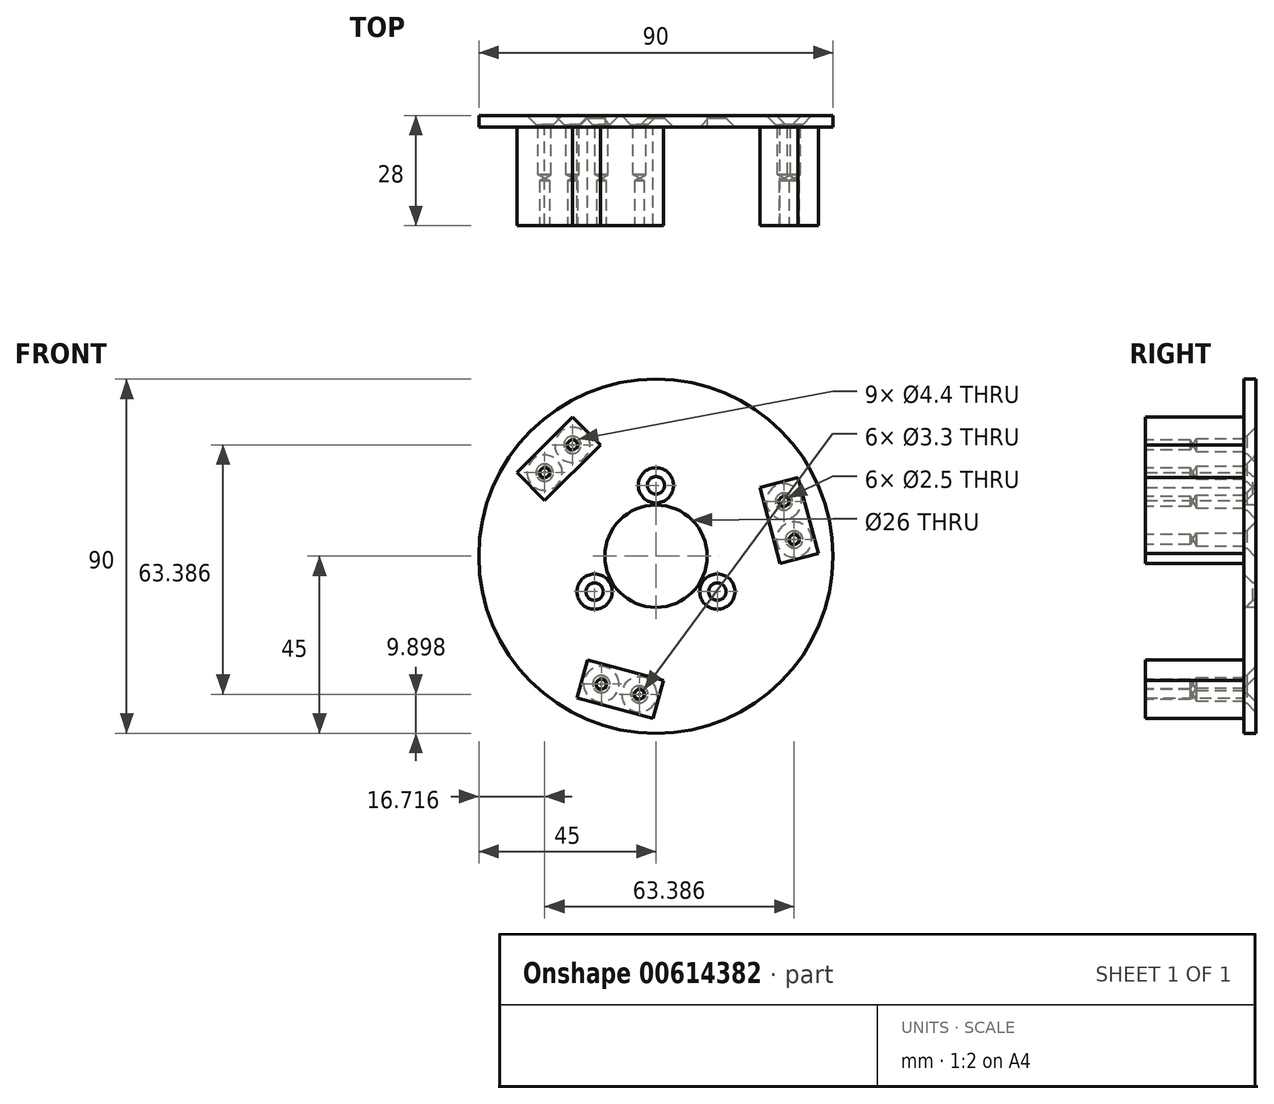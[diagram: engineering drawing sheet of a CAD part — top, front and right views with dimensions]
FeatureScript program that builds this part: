
annotation { "Feature Type Name" : "Feature", "Feature Type Description" : "" }
export const myFeature = defineFeature(function(context is Context, id is Id, definition is map)
    precondition{}
    {
        {
            var Q0;
            Q0=qCreatedBy(makeId("Front.planeOp"),FACE);
            var sketch = newSketch(context, id + "F0", { "sketchPlane" : qUnion([Q0])});
            skCircle(sketch, "E0", {"center": v(0, 0) * mm, "radius": 13 * mm});
            skCircle(sketch, "E1", {"center": v(0, 0) * mm, "radius": 45 * mm});
            skCircle(sketch, "E2", {"center": v(0, 0) * mm, "radius": 23 * mm, "construction": true});
            skLineSegment(sketch, "E3", {"start": v(0, 23) * mm, "end": v(0, 13) * mm, "construction": true});
            skPoint(sketch, "E4", {"position": v(0, 18) * mm});
            skPoint(sketch, "E5.1.0", {"position": v(-15.59, -9) * mm});
            skPoint(sketch, "E5.2.0", {"position": v(15.59, -9) * mm});
            skLineSegment(sketch, "E6", {"start": v(0, 0) * mm, "end": v(-31.82, 31.82) * mm, "construction": true});
            skCircle(sketch, "E7", {"center": v(0, 0) * mm, "radius": 25 * mm, "construction": true});
            skCircle(sketch, "E8", {"center": v(0, 0) * mm, "radius": 18.5 * mm, "construction": true});
            skPoint(sketch, "E9", {"position": v(-21.21, 28.28) * mm});
            skPoint(sketch, "E10.MirrorP", {"position": v(-28.28, 21.21) * mm});
            skLineSegment(sketch, "E11", {"start": v(-28.28, 21.21) * mm, "end": v(-21.21, 28.28) * mm});
            skPoint(sketch, "E12", {"position": v(-24.75, 24.75) * mm});
            skPoint(sketch, "E13.1.0", {"position": v(-9.06, -33.8) * mm});
            skPoint(sketch, "E13.1.1", {"position": v(-13.89, -32.51) * mm});
            skPoint(sketch, "E13.1.2", {"position": v(-4.23, -35.1) * mm});
            skPoint(sketch, "E13.2.0", {"position": v(33.8, 9.06) * mm});
            skPoint(sketch, "E13.2.1", {"position": v(35.1, 4.23) * mm});
            skPoint(sketch, "E13.2.2", {"position": v(32.51, 13.89) * mm});
            skSolve(sketch);
        }
        {
            var Q0;
            Q0=makeQuery(id+"F0.imprint","IMPRINT",FACE,{"disambiguationData":[TD([[makeQuery(id+"F0.imprint","IMPRINT",EDGE,{"derivedFrom":sQuery(id+"F0.wireOp",EDGE,"E0")}),-1.0]])]});
            extrude(context, id + "F1", {"entities" : qUnion([Q0]), "oppositeDirection" : true, "depth" : 3 * mm, "offsetDistance" : 25 * mm});
        }
        {
            var Q0;
            Q0=sQuery(id+"F0.wireOp",VERTEX,"E4");
            var Q1;
            Q1=sQuery(id+"F0.wireOp",VERTEX,"E5.1.0");
            var Q2;
            Q2=sQuery(id+"F0.wireOp",VERTEX,"E5.2.0");
            var Q3;
            Q3=makeQuery(id+"F1.opExtrude","SWEPT_BODY",BODY,{"disambiguationData":[OSD([sQuery(id+"F0.wireOp",EDGE,"E0"),sQuery(id+"F0.wireOp",EDGE,"E1")])]});
            hole(context, id + "F2", {"style" : HoleStyle.C_SINK, "endStyle" : HoleEndStyle.THROUGH, "standardTappedOrClearance" : lookupTablePath({ "standard" : "ISO", "fit" : "Normal", "size" : "M4", "type" : "Clearance" }), "standardBlindInLast" : lookupTablePath({ "fit" : "Standard", "standard" : "ISO", "size" : "M4", "type" : "Clearance" }), "holeDiameter" : 4.4 * mm, "cSinkDiameter" : 8.96 * mm, "cSinkAngle" : 90 * degree, "majorDiameter" : 5 * mm, "isTappedThrough" : true, "tappedDepth" : 12 * mm, "tapClearance" : 3, "locations" : qUnion([Q0, Q1, Q2]), "scope" : qUnion([Q3])});
        }
        {
            var Q0;
            Q0=makeQuery(id+"F1.opExtrude","CAP_FACE",FACE,{"disambiguationData":[OSD([sQuery(id+"F0.wireOp",EDGE,"E0"),sQuery(id+"F0.wireOp",EDGE,"E1")])],"isStart":false});
            var sketch = newSketch(context, id + "F3", { "sketchPlane" : qUnion([Q0])});
            skPoint(sketch, "E14.0", {"position": v(21.21, 28.28) * mm});
            skPoint(sketch, "E15.0", {"position": v(28.28, 21.21) * mm});
            skPoint(sketch, "E16.0", {"position": v(13.89, -32.51) * mm});
            skPoint(sketch, "E17.0", {"position": v(4.23, -35.1) * mm});
            skPoint(sketch, "E18.0", {"position": v(-35.1, 4.23) * mm});
            skPoint(sketch, "E19.0", {"position": v(-32.51, 13.89) * mm});
            skSolve(sketch);
        }
        {
            var Q0;
            Q0=sQuery(id+"F3.wireOp",VERTEX,"E19.0");
            var Q1;
            Q1=sQuery(id+"F3.wireOp",VERTEX,"E18.0");
            var Q2;
            Q2=sQuery(id+"F3.wireOp",VERTEX,"E14.0");
            var Q3;
            Q3=sQuery(id+"F3.wireOp",VERTEX,"E15.0");
            var Q4;
            Q4=sQuery(id+"F3.wireOp",VERTEX,"E16.0");
            var Q5;
            Q5=sQuery(id+"F3.wireOp",VERTEX,"E17.0");
            var Q6;
            Q6=makeQuery(id+"F1.opExtrude","SWEPT_BODY",BODY,{"disambiguationData":[OSD([sQuery(id+"F0.wireOp",EDGE,"E0"),sQuery(id+"F0.wireOp",EDGE,"E1")])]});
            hole(context, id + "F4", {"style" : HoleStyle.C_SINK, "endStyle" : HoleEndStyle.THROUGH, "standardTappedOrClearance" : lookupTablePath({ "standard" : "ISO", "fit" : "Normal", "size" : "M4", "type" : "Clearance" }), "standardBlindInLast" : lookupTablePath({ "fit" : "Standard", "standard" : "ISO", "size" : "M4", "type" : "Clearance" }), "holeDiameter" : 4.4 * mm, "cSinkDiameter" : 8.96 * mm, "cSinkAngle" : 90 * degree, "majorDiameter" : 5 * mm, "isTappedThrough" : true, "tappedDepth" : 12 * mm, "tapClearance" : 3, "locations" : qUnion([Q0, Q1, Q2, Q3, Q4, Q5]), "scope" : qUnion([Q6])});
        }
        {
            var Q0;
            Q0=makeQuery(id+"F0.imprint","IMPRINT",FACE,{"disambiguationData":[TD([[makeQuery(id+"F0.imprint","IMPRINT",EDGE,{"derivedFrom":sQuery(id+"F0.wireOp",EDGE,"E0")}),-1.0]])]});
            var sketch = newSketch(context, id + "F5", { "sketchPlane" : qUnion([Q0])});
            skLineSegment(sketch, "E20", {"start": v(-21.21, 35.36) * mm, "end": v(-35.36, 21.21) * mm});
            skLineSegment(sketch, "E21", {"start": v(-35.36, 21.21) * mm, "end": v(-28.28, 14.14) * mm});
            skLineSegment(sketch, "E22", {"start": v(-28.28, 14.14) * mm, "end": v(-14.14, 28.28) * mm});
            skLineSegment(sketch, "E23", {"start": v(-14.14, 28.28) * mm, "end": v(-21.21, 35.36) * mm});
            skLineSegment(sketch, "E24.0", {"start": v(0, 0) * mm, "end": v(-31.82, 31.82) * mm, "construction": true});
            skSolve(sketch);
        }
        {
            var Q0;
            Q0=makeQuery(id+"F5.imprint","IMPRINT",FACE,{"disambiguationData":[TD([[makeQuery(id+"F5.imprint","IMPRINT",EDGE,{"derivedFrom":sQuery(id+"F5.wireOp",EDGE,"E20")}),1.0]])]});
            extrude(context, id + "F6", {"entities" : qUnion([Q0]), "depth" : 25 * mm, "offsetDistance" : 25 * mm});
        }
        {
            var Q0;
            Q0=makeQuery(id+"F6.opExtrude","CAP_FACE",FACE,{"disambiguationData":[OSD([sQuery(id+"F5.wireOp",EDGE,"E20"),sQuery(id+"F5.wireOp",EDGE,"E21"),sQuery(id+"F5.wireOp",EDGE,"E22"),sQuery(id+"F5.wireOp",EDGE,"E23")])],"isStart":false});
            var sketch = newSketch(context, id + "F7", { "sketchPlane" : qUnion([Q0])});
            skPoint(sketch, "E25.0", {"position": v(-28.28, 21.21) * mm});
            skPoint(sketch, "E26.0", {"position": v(-21.21, 28.28) * mm});
            skSolve(sketch);
        }
        {
            var Q0;
            Q0=sQuery(id+"F0.wireOp",VERTEX,"E10.MirrorP");
            var Q1;
            Q1=sQuery(id+"F0.wireOp",VERTEX,"E9");
            var Q2;
            Q2=makeQuery(id+"F6.opExtrude","SWEPT_BODY",BODY,{"disambiguationData":[OSD([sQuery(id+"F5.wireOp",EDGE,"E20"),sQuery(id+"F5.wireOp",EDGE,"E21"),sQuery(id+"F5.wireOp",EDGE,"E22"),sQuery(id+"F5.wireOp",EDGE,"E23")])]});
            hole(context, id + "F8", {"style" : HoleStyle.SIMPLE, "endStyle" : HoleEndStyle.BLIND, "oppositeDirection" : true, "standardTappedOrClearance" : lookupTablePath({ "standard" : "ISO", "engagement" : "75%", "pitch" : "0.7 mm", "size" : "M4", "type" : "Tapped" }), "standardBlindInLast" : lookupTablePath({ "standard" : "ISO", "engagement" : "75%", "pitch" : "0.7 mm", "size" : "M4", "type" : "Tapped" }), "holeDiameter" : 3.3 * mm, "majorDiameter" : 4 * mm, "showTappedDepth" : true, "holeDepth" : 12 * mm, "isTappedThrough" : true, "tappedDepth" : 9.9 * mm, "tapClearance" : 3, "locations" : qUnion([Q0, Q1]), "scope" : qUnion([Q2])});
        }
        {
            var Q0;
            Q0=sQuery(id+"F7.wireOp",VERTEX,"E25.0");
            var Q1;
            Q1=sQuery(id+"F7.wireOp",VERTEX,"E26.0");
            var Q2;
            Q2=makeQuery(id+"F6.opExtrude","SWEPT_BODY",BODY,{"disambiguationData":[OSD([sQuery(id+"F5.wireOp",EDGE,"E20"),sQuery(id+"F5.wireOp",EDGE,"E21"),sQuery(id+"F5.wireOp",EDGE,"E22"),sQuery(id+"F5.wireOp",EDGE,"E23")])]});
            hole(context, id + "F9", {"style" : HoleStyle.SIMPLE, "endStyle" : HoleEndStyle.BLIND, "standardTappedOrClearance" : lookupTablePath({ "standard" : "ISO", "engagement" : "75%", "pitch" : "0.5 mm", "size" : "M3", "type" : "Tapped" }), "standardBlindInLast" : lookupTablePath({ "standard" : "ISO", "engagement" : "75%", "pitch" : "0.5 mm", "size" : "M3", "type" : "Tapped" }), "holeDiameter" : 2.5 * mm, "majorDiameter" : 3 * mm, "showTappedDepth" : true, "holeDepth" : 11.4 * mm, "isTappedThrough" : true, "tappedDepth" : 9.9 * mm, "tapClearance" : 3, "locations" : qUnion([Q0, Q1]), "scope" : qUnion([Q2])});
        }
        {
            var Q0;
            Q0=makeQuery(id+"F6.opExtrude","SWEPT_BODY",BODY,{"disambiguationData":[OSD([sQuery(id+"F5.wireOp",EDGE,"E20"),sQuery(id+"F5.wireOp",EDGE,"E21"),sQuery(id+"F5.wireOp",EDGE,"E22"),sQuery(id+"F5.wireOp",EDGE,"E23")])]});
            var Q1;
            Q1=makeQuery(id+"F1.opExtrude","SWEPT_FACE",FACE,{"disambiguationData":[OSD([sQuery(id+"F0.wireOp",EDGE,"E0")])]});
            circularPattern(context, id + "F10", {"entities" : qUnion([Q0]), "axis" : qUnion([Q1]), "angle" : 360 * degree, "instanceCount" : 3, "equalSpace" : true});
        }
    });
